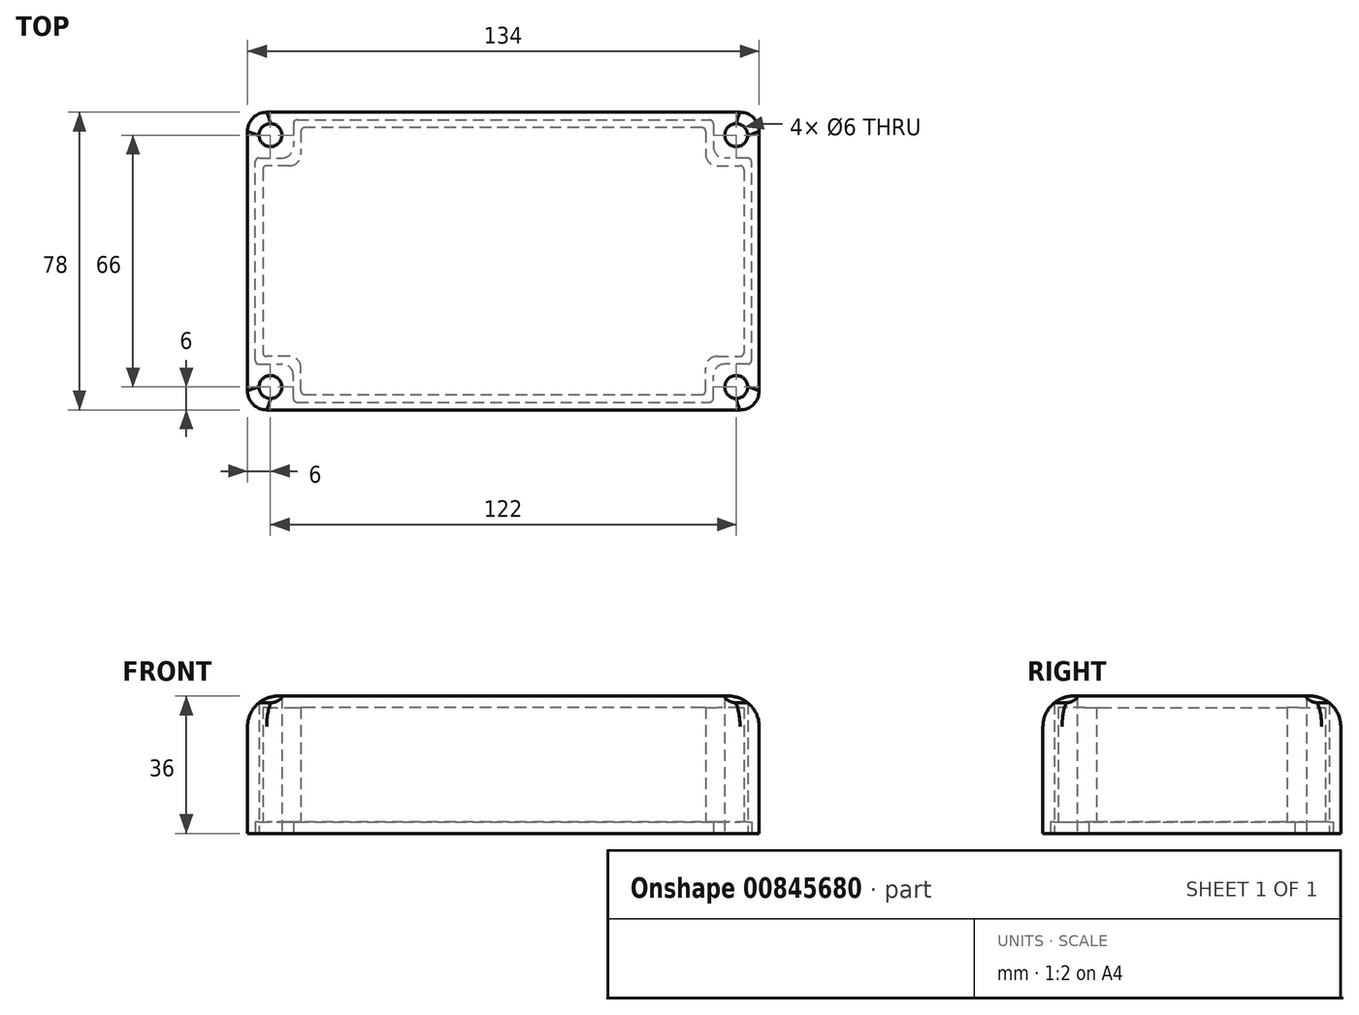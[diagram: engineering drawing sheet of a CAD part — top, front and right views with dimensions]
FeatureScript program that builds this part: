
annotation { "Feature Type Name" : "Feature", "Feature Type Description" : "" }
export const myFeature = defineFeature(function(context is Context, id is Id, definition is map)
    precondition{}
    {
        {
            var Q0;
            Q0=qCreatedBy(makeId("Top.planeOp"),FACE);
            var sketch = newSketch(context, id + "F0", { "sketchPlane" : qUnion([Q0])});
            skLineSegment(sketch, "E0.bottom", {"start": v(-67, 39) * mm, "end": v(67, 39) * mm});
            skLineSegment(sketch, "E0.top", {"start": v(-67, -39) * mm, "end": v(67, -39) * mm});
            skLineSegment(sketch, "E0.left", {"start": v(-67, 39) * mm, "end": v(-67, -39) * mm});
            skLineSegment(sketch, "E0.right", {"start": v(67, 39) * mm, "end": v(67, -39) * mm});
            skSolve(sketch);
        }
        {
            var Q0;
            Q0 = qSketchRegion(id + "F0", true);
            extrude(context, id + "F1", {"entities" : qUnion([Q0]), "depth" : 36 * mm, "offsetDistance" : 25 * mm});
        }
        {
            var Q0;
            Q0=makeQuery(id+"F1.opExtrude","CAP_FACE",FACE,{"disambiguationData":[OSD([sQuery(id+"F0.wireOp",EDGE,"E0.bottom"),sQuery(id+"F0.wireOp",EDGE,"E0.top"),sQuery(id+"F0.wireOp",EDGE,"E0.left"),sQuery(id+"F0.wireOp",EDGE,"E0.right")])],"isStart":true});
            var sketch = newSketch(context, id + "F2", { "sketchPlane" : qUnion([Q0])});
            skLineSegment(sketch, "E1", {"start": v(-63, 24) * mm, "end": v(-63, -24) * mm});
            skLineSegment(sketch, "E2", {"start": v(-62, 25) * mm, "end": v(-56, 25) * mm});
            skLineSegment(sketch, "E3", {"start": v(-53, 28) * mm, "end": v(-53, 34) * mm});
            skLineSegment(sketch, "E4", {"start": v(-52, 35) * mm, "end": v(0, 35) * mm});
            skLineSegment(sketch, "E5", {"start": v(-62, -25) * mm, "end": v(-56, -25) * mm});
            skLineSegment(sketch, "E6", {"start": v(-53, -28) * mm, "end": v(-53, -34) * mm});
            skLineSegment(sketch, "E7", {"start": v(-52, -35) * mm, "end": v(0, -35) * mm});
            skLineSegment(sketch, "E8", {"start": v(0, 43.07) * mm, "end": v(0, -54.36) * mm, "construction": true});
            skLineSegment(sketch, "E9.MirrorCS", {"start": v(52, 35) * mm, "end": v(0, 35) * mm});
            skLineSegment(sketch, "E10.MirrorCS", {"start": v(53, 28) * mm, "end": v(53, 34) * mm});
            skLineSegment(sketch, "E11.MirrorCS", {"start": v(62, 25) * mm, "end": v(56, 25) * mm});
            skLineSegment(sketch, "E12.MirrorCS", {"start": v(63, 24) * mm, "end": v(63, -24) * mm});
            skLineSegment(sketch, "E13.MirrorCS", {"start": v(62, -25) * mm, "end": v(56, -25) * mm});
            skLineSegment(sketch, "E14.MirrorCS", {"start": v(53, -28) * mm, "end": v(53, -34) * mm});
            skLineSegment(sketch, "E15.MirrorCS", {"start": v(52, -35) * mm, "end": v(0, -35) * mm});
            skPoint(sketch, "E16.visualSharp", {"position": v(-63, 25) * mm});
            skArc(sketch, "E16.filletArc", {"start": v(-62, 25) * mm, "mid": v(-62.7, 24.7) * mm, "end": v(-63, 24) * mm});
            skPoint(sketch, "E17.visualSharp", {"position": v(-53, 35) * mm});
            skArc(sketch, "E17.filletArc", {"start": v(-52, 35) * mm, "mid": v(-52.7, 34.7) * mm, "end": v(-53, 34) * mm});
            skPoint(sketch, "E18.visualSharp", {"position": v(53, 35) * mm});
            skArc(sketch, "E18.filletArc", {"start": v(53, 34) * mm, "mid": v(52.7, 34.7) * mm, "end": v(52, 35) * mm});
            skPoint(sketch, "E19.visualSharp", {"position": v(63, 25) * mm});
            skArc(sketch, "E19.filletArc", {"start": v(63, 24) * mm, "mid": v(62.7, 24.7) * mm, "end": v(62, 25) * mm});
            skPoint(sketch, "E20.visualSharp", {"position": v(63, -25) * mm});
            skArc(sketch, "E20.filletArc", {"start": v(62, -25) * mm, "mid": v(62.7, -24.7) * mm, "end": v(63, -24) * mm});
            skPoint(sketch, "E21.visualSharp", {"position": v(53, -35) * mm});
            skArc(sketch, "E21.filletArc", {"start": v(52, -35) * mm, "mid": v(52.7, -34.7) * mm, "end": v(53, -34) * mm});
            skPoint(sketch, "E22.visualSharp", {"position": v(-53, -35) * mm});
            skArc(sketch, "E22.filletArc", {"start": v(-53, -34) * mm, "mid": v(-52.7, -34.7) * mm, "end": v(-52, -35) * mm});
            skPoint(sketch, "E23.visualSharp", {"position": v(-63, -25) * mm});
            skArc(sketch, "E23.filletArc", {"start": v(-63, -24) * mm, "mid": v(-62.7, -24.7) * mm, "end": v(-62, -25) * mm});
            skPoint(sketch, "E24.visualSharp", {"position": v(-53, 25) * mm});
            skArc(sketch, "E24.filletArc", {"start": v(-56, 25) * mm, "mid": v(-53.88, 25.88) * mm, "end": v(-53, 28) * mm});
            skPoint(sketch, "E25.visualSharp", {"position": v(53, 25) * mm});
            skArc(sketch, "E25.filletArc", {"start": v(53, 28) * mm, "mid": v(53.88, 25.88) * mm, "end": v(56, 25) * mm});
            skPoint(sketch, "E26.visualSharp", {"position": v(53, -25) * mm});
            skArc(sketch, "E26.filletArc", {"start": v(56, -25) * mm, "mid": v(53.88, -25.88) * mm, "end": v(53, -28) * mm});
            skPoint(sketch, "E27.visualSharp", {"position": v(-53, -25) * mm});
            skArc(sketch, "E27.filletArc", {"start": v(-53, -28) * mm, "mid": v(-53.88, -25.88) * mm, "end": v(-56, -25) * mm});
            skSolve(sketch);
        }
        {
            var Q0;
            Q0 = qSketchRegion(id + "F2", true);
            extrude(context, id + "F3", {"entities" : qUnion([Q0]), "operationType" : NewBodyOperationType.REMOVE, "oppositeDirection" : true, "depth" : 33 * mm, "offsetDistance" : 25 * mm});
        }
        {
            var Q0;
            Q0=makeQuery(id+"F1.opExtrude","CAP_FACE",FACE,{"disambiguationData":[OSD([sQuery(id+"F0.wireOp",EDGE,"E0.bottom"),sQuery(id+"F0.wireOp",EDGE,"E0.top"),sQuery(id+"F0.wireOp",EDGE,"E0.left"),sQuery(id+"F0.wireOp",EDGE,"E0.right")])],"isStart":true});
            var sketch = newSketch(context, id + "F4", { "sketchPlane" : qUnion([Q0])});
            skLineSegment(sketch, "E28.bottom", {"start": v(-54, 37) * mm, "end": v(54, 37) * mm});
            skLineSegment(sketch, "E28.top", {"start": v(-54, -37) * mm, "end": v(54, -37) * mm});
            skLineSegment(sketch, "E28.left", {"start": v(-65, 26) * mm, "end": v(-65, -26) * mm});
            skLineSegment(sketch, "E28.right", {"start": v(65, 26) * mm, "end": v(65, -26) * mm});
            skLineSegment(sketch, "E29.top", {"start": v(-64, 27) * mm, "end": v(-58, 27) * mm});
            skLineSegment(sketch, "E29.right", {"start": v(-55, 36) * mm, "end": v(-55, 30) * mm});
            skLineSegment(sketch, "E30", {"start": v(-19.44, 0) * mm, "end": v(15.59, 0) * mm});
            skLineSegment(sketch, "E31", {"start": v(0, 20.06) * mm, "end": v(0, -12.53) * mm, "construction": true});
            skLineSegment(sketch, "E32.MirrorCS", {"start": v(-64, -27) * mm, "end": v(-58, -27) * mm});
            skLineSegment(sketch, "E33.MirrorCS", {"start": v(-55, -36) * mm, "end": v(-55, -30) * mm});
            skLineSegment(sketch, "E34.MirrorCS", {"start": v(55, 36) * mm, "end": v(55, 30) * mm});
            skLineSegment(sketch, "E35.MirrorCS", {"start": v(64, 27) * mm, "end": v(58, 27) * mm});
            skLineSegment(sketch, "E36.MirrorCS", {"start": v(64, -27) * mm, "end": v(58, -27) * mm});
            skLineSegment(sketch, "E37.MirrorCS", {"start": v(55, -36) * mm, "end": v(55, -30) * mm});
            skPoint(sketch, "E38.visualSharp", {"position": v(-55, 27) * mm});
            skArc(sketch, "E38.filletArc", {"start": v(-58, 27) * mm, "mid": v(-55.88, 27.88) * mm, "end": v(-55, 30) * mm});
            skPoint(sketch, "E39.visualSharp", {"position": v(-55, -27) * mm});
            skArc(sketch, "E39.filletArc", {"start": v(-55, -30) * mm, "mid": v(-55.88, -27.88) * mm, "end": v(-58, -27) * mm});
            skPoint(sketch, "E40.visualSharp", {"position": v(55, -27) * mm});
            skArc(sketch, "E40.filletArc", {"start": v(58, -27) * mm, "mid": v(55.88, -27.88) * mm, "end": v(55, -30) * mm});
            skPoint(sketch, "E41.visualSharp", {"position": v(55, 27) * mm});
            skArc(sketch, "E41.filletArc", {"start": v(55, 30) * mm, "mid": v(55.88, 27.88) * mm, "end": v(58, 27) * mm});
            skPoint(sketch, "E42.visualSharp", {"position": v(-55, 37) * mm});
            skArc(sketch, "E42.filletArc", {"start": v(-54, 37) * mm, "mid": v(-54.7, 36.7) * mm, "end": v(-55, 36) * mm});
            skPoint(sketch, "E43.visualSharp", {"position": v(-65, 27) * mm});
            skArc(sketch, "E43.filletArc", {"start": v(-64, 27) * mm, "mid": v(-64.7, 26.7) * mm, "end": v(-65, 26) * mm});
            skPoint(sketch, "E44.visualSharp", {"position": v(-65, -27) * mm});
            skArc(sketch, "E44.filletArc", {"start": v(-65, -26) * mm, "mid": v(-64.7, -26.7) * mm, "end": v(-64, -27) * mm});
            skPoint(sketch, "E45.visualSharp", {"position": v(-55, -37) * mm});
            skArc(sketch, "E45.filletArc", {"start": v(-55, -36) * mm, "mid": v(-54.7, -36.7) * mm, "end": v(-54, -37) * mm});
            skPoint(sketch, "E46.visualSharp", {"position": v(55, -37) * mm});
            skArc(sketch, "E46.filletArc", {"start": v(54, -37) * mm, "mid": v(54.7, -36.7) * mm, "end": v(55, -36) * mm});
            skPoint(sketch, "E47.visualSharp", {"position": v(65, -27) * mm});
            skArc(sketch, "E47.filletArc", {"start": v(64, -27) * mm, "mid": v(64.7, -26.7) * mm, "end": v(65, -26) * mm});
            skPoint(sketch, "E48.visualSharp", {"position": v(65, 27) * mm});
            skArc(sketch, "E48.filletArc", {"start": v(65, 26) * mm, "mid": v(64.7, 26.7) * mm, "end": v(64, 27) * mm});
            skPoint(sketch, "E49.visualSharp", {"position": v(55, 37) * mm});
            skArc(sketch, "E49.filletArc", {"start": v(55, 36) * mm, "mid": v(54.7, 36.7) * mm, "end": v(54, 37) * mm});
            skSolve(sketch);
        }
        {
            var Q0;
            Q0 = qSketchRegion(id + "F4", true);
            extrude(context, id + "F5", {"entities" : qUnion([Q0]), "operationType" : NewBodyOperationType.REMOVE, "oppositeDirection" : true, "depth" : 3 * mm, "offsetDistance" : 25 * mm});
        }
        {
            var Q0;
            Q0=makeQuery(id+"F1.opExtrude","SWEPT_EDGE",EDGE,{"disambiguationData":[OSD([sQuery(id+"F0.wireOp",EDGE,"E0.top"),sQuery(id+"F0.wireOp",EDGE,"E0.left")])]});
            var Q1;
            Q1=makeQuery(id+"F1.opExtrude","SWEPT_EDGE",EDGE,{"disambiguationData":[OSD([sQuery(id+"F0.wireOp",EDGE,"E0.top"),sQuery(id+"F0.wireOp",EDGE,"E0.right")])]});
            var Q2;
            Q2=makeQuery(id+"F1.opExtrude","SWEPT_EDGE",EDGE,{"disambiguationData":[OSD([sQuery(id+"F0.wireOp",EDGE,"E0.bottom"),sQuery(id+"F0.wireOp",EDGE,"E0.right")])]});
            var Q3;
            Q3=makeQuery(id+"F1.opExtrude","SWEPT_EDGE",EDGE,{"disambiguationData":[OSD([sQuery(id+"F0.wireOp",EDGE,"E0.bottom"),sQuery(id+"F0.wireOp",EDGE,"E0.left")])]});
            fillet(context, id + "F6", {"entities" : qUnion([Q0, Q1, Q2, Q3]), "radius" : 5 * mm, "tangentPropagation" : true, "allowEdgeOverflow" : false});
        }
        {
            var Q0;
            Q0=makeQuery(id+"F1.opExtrude","CAP_FACE",FACE,{"disambiguationData":[OSD([sQuery(id+"F0.wireOp",EDGE,"E0.bottom"),sQuery(id+"F0.wireOp",EDGE,"E0.top"),sQuery(id+"F0.wireOp",EDGE,"E0.left"),sQuery(id+"F0.wireOp",EDGE,"E0.right")])],"isStart":true});
            var sketch = newSketch(context, id + "F7", { "sketchPlane" : qUnion([Q0])});
            skCircle(sketch, "E50", {"center": v(-61, -33) * mm, "radius": 3 * mm});
            skLineSegment(sketch, "E51", {"start": v(-16.51, 0) * mm, "end": v(24.31, 0) * mm, "construction": true});
            skLineSegment(sketch, "E52", {"start": v(0, 20.96) * mm, "end": v(0, -16.06) * mm, "construction": true});
            skPoint(sketch, "E52.startSnap0", {"position": v(0, 37) * mm});
            skCircle(sketch, "E53.MirrorC", {"center": v(-61, 33) * mm, "radius": 3 * mm});
            skCircle(sketch, "E54.MirrorC", {"center": v(61, 33) * mm, "radius": 3 * mm});
            skCircle(sketch, "E55.MirrorC", {"center": v(61, -33) * mm, "radius": 3 * mm});
            skSolve(sketch);
        }
        {
            var Q0;
            Q0 = qSketchRegion(id + "F7", true);
            extrude(context, id + "F8", {"entities" : qUnion([Q0]), "operationType" : NewBodyOperationType.REMOVE, "oppositeDirection" : true, "depth" : 42.1 * mm, "offsetDistance" : 25 * mm});
        }
        {
            var Q0;
            Q0=makeQuery(id+"F1.opExtrude","CAP_EDGE",EDGE,{"disambiguationData":[OSD([sQuery(id+"F0.wireOp",EDGE,"E0.top")])],"isStart":false});
            fillet(context, id + "F9", {"entities" : qUnion([Q0]), "radius" : 8 * mm, "tangentPropagation" : true, "allowEdgeOverflow" : false});
        }
    });
